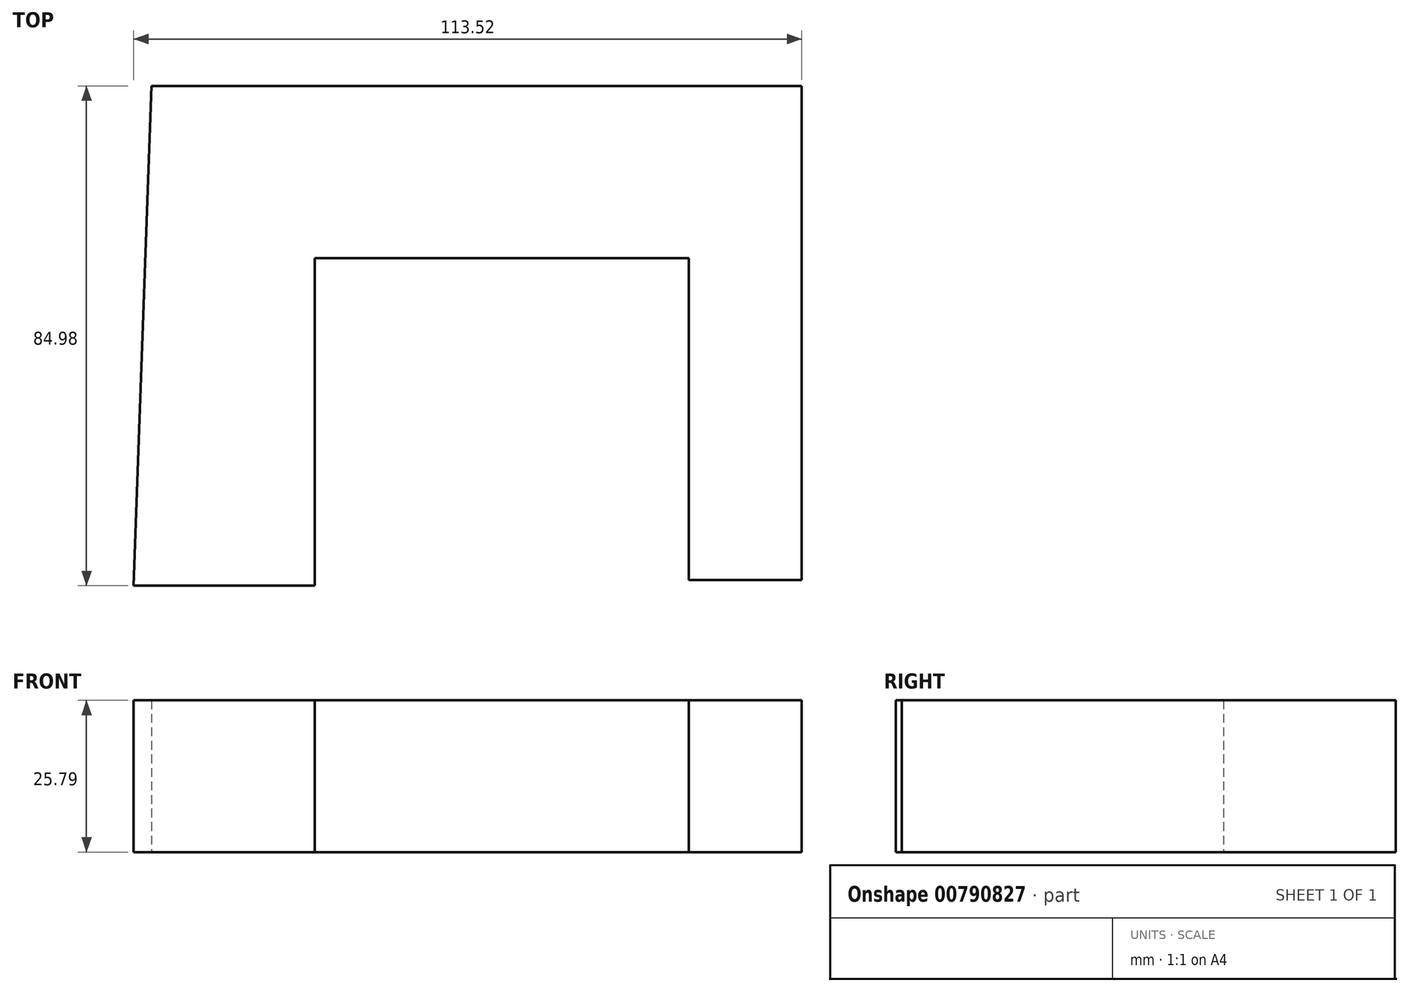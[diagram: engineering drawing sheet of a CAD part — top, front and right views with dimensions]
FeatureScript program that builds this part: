
annotation { "Feature Type Name" : "Feature", "Feature Type Description" : "" }
export const myFeature = defineFeature(function(context is Context, id is Id, definition is map)
    precondition{}
    {
        {
            var Q0;
            Q0=qCreatedBy(makeId("Top.planeOp"),FACE);
            var sketch = newSketch(context, id + "F0", { "sketchPlane" : qUnion([Q0])});
            skLineSegment(sketch, "E0", {"start": v(-53.23, 46.12) * mm, "end": v(57.25, 46.12) * mm});
            skLineSegment(sketch, "E1", {"start": v(57.25, 46.12) * mm, "end": v(57.25, -37.87) * mm});
            skLineSegment(sketch, "E2", {"start": v(57.25, -37.87) * mm, "end": v(38.06, -37.87) * mm});
            skLineSegment(sketch, "E3", {"start": v(38.06, -37.87) * mm, "end": v(38.06, 16.84) * mm});
            skLineSegment(sketch, "E4", {"start": v(38.06, 16.84) * mm, "end": v(-25.48, 16.84) * mm});
            skLineSegment(sketch, "E5", {"start": v(-25.48, 16.84) * mm, "end": v(-25.48, -31.69) * mm});
            skLineSegment(sketch, "E6", {"start": v(-25.48, -31.69) * mm, "end": v(-25.48, -38.86) * mm});
            skLineSegment(sketch, "E7", {"start": v(-25.48, -38.86) * mm, "end": v(-47.53, -38.86) * mm});
            skLineSegment(sketch, "E8", {"start": v(-47.53, -38.86) * mm, "end": v(-56.27, -38.86) * mm});
            skLineSegment(sketch, "E9", {"start": v(-56.27, -38.86) * mm, "end": v(-53.23, 46.12) * mm});
            skSolve(sketch);
        }
        {
            var Q0;
            Q0=makeQuery(id+"F0.imprint","IMPRINT",FACE,{"disambiguationData":[TD([[makeQuery(id+"F0.imprint","IMPRINT",EDGE,{"derivedFrom":sQuery(id+"F0.wireOp",EDGE,"E0")}),-1.0]])]});
            extrude(context, id + "F1", {"entities" : qUnion([Q0]), "depth" : 25.8 * mm, "offsetDistance" : 25.4 * mm});
        }
    });
